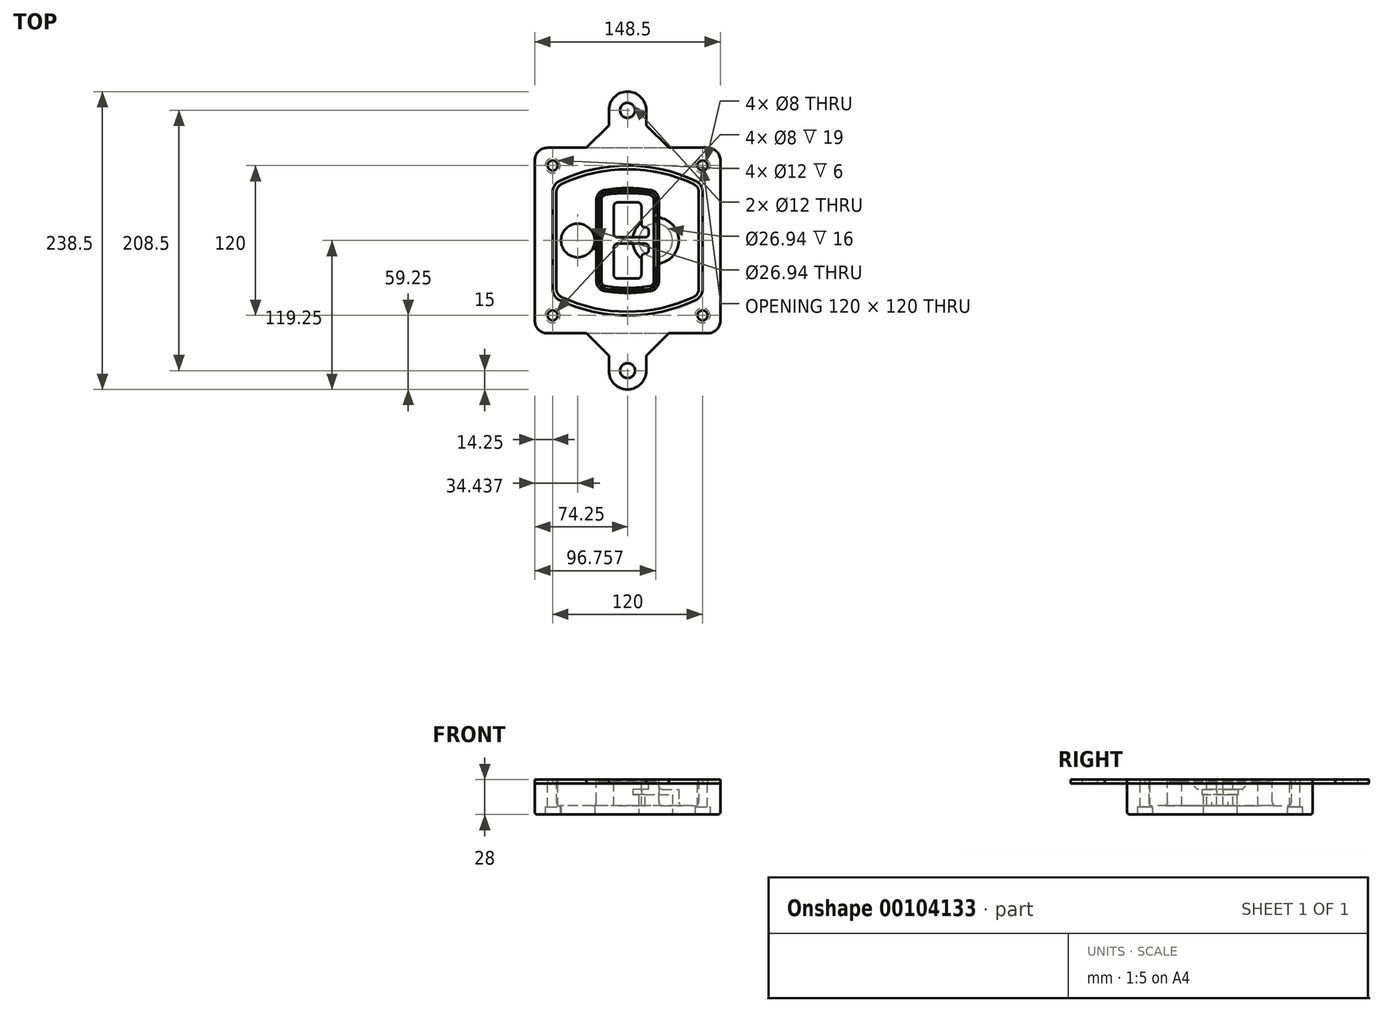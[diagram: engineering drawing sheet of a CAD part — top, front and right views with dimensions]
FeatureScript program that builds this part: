
annotation { "Feature Type Name" : "Feature", "Feature Type Description" : "" }
export const myFeature = defineFeature(function(context is Context, id is Id, definition is map)
    precondition{}
    {
        {
            var Q0;
            Q0=qCreatedBy(makeId("Top.planeOp"),FACE);
            var sketch = newSketch(context, id + "F0", { "sketchPlane" : qUnion([Q0])});
            skPoint(sketch, "E0.rect.middle", {"position": v(0, 0) * mm});
            skLineSegment(sketch, "E1.bottom", {"start": v(-64.25, -74.25) * mm, "end": v(64.25, -74.25) * mm});
            skLineSegment(sketch, "E1.top", {"start": v(-64.25, 74.25) * mm, "end": v(64.25, 74.25) * mm});
            skLineSegment(sketch, "E1.left", {"start": v(-74.25, -64.25) * mm, "end": v(-74.25, 64.25) * mm});
            skLineSegment(sketch, "E1.right", {"start": v(74.25, -64.25) * mm, "end": v(74.25, 64.25) * mm});
            skLineSegment(sketch, "E2", {"start": v(-74.25, 74.25) * mm, "end": v(74.25, -74.25) * mm, "construction": true});
            skLineSegment(sketch, "E3", {"start": v(74.25, 74.25) * mm, "end": v(-74.25, -74.25) * mm, "construction": true});
            skCircle(sketch, "E4", {"center": v(-60, 60) * mm, "radius": 4 * mm});
            skCircle(sketch, "E5", {"center": v(60, 60) * mm, "radius": 4 * mm});
            skCircle(sketch, "E6", {"center": v(60, -60) * mm, "radius": 4 * mm});
            skCircle(sketch, "E7", {"center": v(-60, -60) * mm, "radius": 4 * mm});
            skLineSegment(sketch, "E8", {"start": v(-60, 60) * mm, "end": v(60, 60) * mm, "construction": true});
            skLineSegment(sketch, "E9", {"start": v(60, 60) * mm, "end": v(60, -60) * mm, "construction": true});
            skLineSegment(sketch, "E10", {"start": v(60, -60) * mm, "end": v(-60, -60) * mm, "construction": true});
            skLineSegment(sketch, "E11", {"start": v(-60, -60) * mm, "end": v(-60, 60) * mm, "construction": true});
            skLineSegment(sketch, "E12", {"start": v(-60, 38.83) * mm, "end": v(-60, -38.83) * mm});
            skLineSegment(sketch, "E13", {"start": v(60, 38.83) * mm, "end": v(60, -38.83) * mm});
            skArc(sketch, "E14", {"start": v(54.26, 47.88) * mm, "mid": v(0, 60) * mm, "end": v(-54.26, 47.88) * mm});
            skArc(sketch, "E15", {"start": v(-54.26, -47.88) * mm, "mid": v(0, -60) * mm, "end": v(54.26, -47.88) * mm});
            skLineSegment(sketch, "E16", {"start": v(-60, 0) * mm, "end": v(60, 0) * mm, "construction": true});
            skPoint(sketch, "E17.visualSharp", {"position": v(-60, -45) * mm});
            skArc(sketch, "E17.filletArc", {"start": v(-60, -38.83) * mm, "mid": v(-58.44, -44.2) * mm, "end": v(-54.26, -47.88) * mm});
            skPoint(sketch, "E18.visualSharp", {"position": v(-60, 45) * mm});
            skArc(sketch, "E18.filletArc", {"start": v(-54.26, 47.88) * mm, "mid": v(-58.44, 44.2) * mm, "end": v(-60, 38.83) * mm});
            skPoint(sketch, "E19.visualSharp", {"position": v(60, 45) * mm});
            skArc(sketch, "E19.filletArc", {"start": v(60, 38.83) * mm, "mid": v(58.44, 44.2) * mm, "end": v(54.26, 47.88) * mm});
            skPoint(sketch, "E20.visualSharp", {"position": v(60, -45) * mm});
            skArc(sketch, "E20.filletArc", {"start": v(54.26, -47.88) * mm, "mid": v(58.44, -44.2) * mm, "end": v(60, -38.83) * mm});
            skPoint(sketch, "E21.visualSharp", {"position": v(-74.25, 74.25) * mm});
            skArc(sketch, "E21.filletArc", {"start": v(-64.25, 74.25) * mm, "mid": v(-71.32, 71.32) * mm, "end": v(-74.25, 64.25) * mm});
            skPoint(sketch, "E22.visualSharp", {"position": v(74.25, 74.25) * mm});
            skArc(sketch, "E22.filletArc", {"start": v(74.25, 64.25) * mm, "mid": v(71.32, 71.32) * mm, "end": v(64.25, 74.25) * mm});
            skPoint(sketch, "E23.visualSharp", {"position": v(74.25, -74.25) * mm});
            skArc(sketch, "E23.filletArc", {"start": v(64.25, -74.25) * mm, "mid": v(71.32, -71.32) * mm, "end": v(74.25, -64.25) * mm});
            skPoint(sketch, "E24.visualSharp", {"position": v(-74.25, -74.25) * mm});
            skArc(sketch, "E24.filletArc", {"start": v(-74.25, -64.25) * mm, "mid": v(-71.32, -71.32) * mm, "end": v(-64.25, -74.25) * mm});
            skArc(sketch, "E25.0", {"start": v(57, 38.83) * mm, "mid": v(55.9, 42.58) * mm, "end": v(52.98, 45.17) * mm});
            skLineSegment(sketch, "E25.1", {"start": v(57, 38.83) * mm, "end": v(57, -38.83) * mm});
            skArc(sketch, "E25.2", {"start": v(52.98, -45.17) * mm, "mid": v(55.9, -42.58) * mm, "end": v(57, -38.83) * mm});
            skArc(sketch, "E25.3", {"start": v(-52.98, -45.17) * mm, "mid": v(0, -57) * mm, "end": v(52.98, -45.17) * mm});
            skArc(sketch, "E25.4", {"start": v(-57, -38.83) * mm, "mid": v(-55.9, -42.58) * mm, "end": v(-52.98, -45.17) * mm});
            skArc(sketch, "E25.5", {"start": v(52.98, 45.17) * mm, "mid": v(0, 57) * mm, "end": v(-52.98, 45.17) * mm});
            skLineSegment(sketch, "E25.6", {"start": v(-57, 38.83) * mm, "end": v(-57, -38.83) * mm});
            skArc(sketch, "E25.7", {"start": v(-52.98, 45.17) * mm, "mid": v(-55.9, 42.58) * mm, "end": v(-57, 38.83) * mm});
            skArc(sketch, "E26.0", {"start": v(-55.96, 51.5) * mm, "mid": v(-61.82, 46.33) * mm, "end": v(-64, 38.83) * mm});
            skArc(sketch, "E26.1", {"start": v(55.96, 51.5) * mm, "mid": v(0, 64) * mm, "end": v(-55.96, 51.5) * mm});
            skArc(sketch, "E26.2", {"start": v(64, 38.83) * mm, "mid": v(61.82, 46.33) * mm, "end": v(55.96, 51.5) * mm});
            skLineSegment(sketch, "E26.3", {"start": v(64, 38.83) * mm, "end": v(64, -38.83) * mm});
            skArc(sketch, "E26.4", {"start": v(55.96, -51.5) * mm, "mid": v(61.82, -46.33) * mm, "end": v(64, -38.83) * mm});
            skLineSegment(sketch, "E26.5", {"start": v(-64, 38.83) * mm, "end": v(-64, -38.83) * mm});
            skArc(sketch, "E26.6", {"start": v(-55.96, -51.5) * mm, "mid": v(0, -64) * mm, "end": v(55.96, -51.5) * mm});
            skArc(sketch, "E26.7", {"start": v(-64, -38.83) * mm, "mid": v(-61.82, -46.33) * mm, "end": v(-55.96, -51.5) * mm});
            skSolve(sketch);
        }
        {
            var Q0;
            Q0=makeQuery(id+"F0.imprint","IMPRINT",FACE,{"disambiguationData":[TD([[makeQuery(id+"F0.imprint","IMPRINT",EDGE,{"derivedFrom":sQuery(id+"F0.wireOp",EDGE,"E1.bottom")}),1.0]])]});
            var Q1;
            Q1=makeQuery(id+"F0.imprint","IMPRINT",FACE,{"disambiguationData":[TD([[makeQuery(id+"F0.imprint","IMPRINT",EDGE,{"derivedFrom":sQuery(id+"F0.wireOp",EDGE,"E12")}),1.0]])]});
            var Q2;
            Q2=makeQuery(id+"F0.imprint","IMPRINT",FACE,{"disambiguationData":[TD([[makeQuery(id+"F0.imprint","IMPRINT",EDGE,{"derivedFrom":sQuery(id+"F0.wireOp",EDGE,"E25.0")}),1.0]])]});
            var Q3;
            Q3=makeQuery(id+"F0.imprint","IMPRINT",FACE,{"disambiguationData":[TD([[makeQuery(id+"F0.imprint","IMPRINT",EDGE,{"derivedFrom":sQuery(id+"F0.wireOp",EDGE,"E12")}),-1.0]])]});
            extrude(context, id + "F1", {"entities" : qUnion([Q0, Q1, Q2, Q3]), "oppositeDirection" : true, "depth" : 25 * mm});
        }
        {
            var Q0;
            Q0=makeQuery(id+"F0.imprint","IMPRINT",FACE,{"disambiguationData":[TD([[makeQuery(id+"F0.imprint","IMPRINT",EDGE,{"derivedFrom":sQuery(id+"F0.wireOp",EDGE,"E12")}),1.0]])]});
            extrude(context, id + "F2", {"entities" : qUnion([Q0]), "operationType" : NewBodyOperationType.ADD, "depth" : 3 * mm});
        }
        {
            var Q0;
            Q0=makeQuery(id+"F0.imprint","IMPRINT",FACE,{"disambiguationData":[TD([[makeQuery(id+"F0.imprint","IMPRINT",EDGE,{"derivedFrom":sQuery(id+"F0.wireOp",EDGE,"E25.0")}),1.0]])]});
            extrude(context, id + "F3", {"entities" : qUnion([Q0]), "operationType" : NewBodyOperationType.REMOVE, "oppositeDirection" : true, "depth" : 18 * mm});
        }
        {
            var Q0;
            Q0=makeQuery(id+"F2.opExtrude","CAP_FACE",FACE,{"disambiguationData":[OSD([sQuery(id+"F0.wireOp",EDGE,"E12"),sQuery(id+"F0.wireOp",EDGE,"E13"),sQuery(id+"F0.wireOp",EDGE,"E14"),sQuery(id+"F0.wireOp",EDGE,"E15"),sQuery(id+"F0.wireOp",EDGE,"E17.filletArc"),sQuery(id+"F0.wireOp",EDGE,"E18.filletArc"),sQuery(id+"F0.wireOp",EDGE,"E19.filletArc"),sQuery(id+"F0.wireOp",EDGE,"E20.filletArc"),sQuery(id+"F0.wireOp",EDGE,"E25.0"),sQuery(id+"F0.wireOp",EDGE,"E25.1"),sQuery(id+"F0.wireOp",EDGE,"E25.2"),sQuery(id+"F0.wireOp",EDGE,"E25.3"),sQuery(id+"F0.wireOp",EDGE,"E25.4"),sQuery(id+"F0.wireOp",EDGE,"E25.5"),sQuery(id+"F0.wireOp",EDGE,"E25.6"),sQuery(id+"F0.wireOp",EDGE,"E25.7")])],"isStart":false});
            var sketch = newSketch(context, id + "F4", { "sketchPlane" : qUnion([Q0])});
            skArc(sketch, "E27.0", {"start": v(-18.34, -40.45) * mm, "mid": v(0, -42) * mm, "end": v(18.34, -40.45) * mm});
            skArc(sketch, "E28.0", {"start": v(18.34, 40.45) * mm, "mid": v(0, 42) * mm, "end": v(-18.34, 40.45) * mm});
            skLineSegment(sketch, "E29", {"start": v(-25, 32.57) * mm, "end": v(-25, -32.57) * mm});
            skLineSegment(sketch, "E30", {"start": v(25, 32.57) * mm, "end": v(25, -32.57) * mm});
            skLineSegment(sketch, "E31", {"start": v(-25, 39.1) * mm, "end": v(25, 39.1) * mm, "construction": true});
            skLineSegment(sketch, "E32", {"start": v(-25, -39.1) * mm, "end": v(25, -39.1) * mm, "construction": true});
            skPoint(sketch, "E33.visualSharp", {"position": v(-25, 39.1) * mm});
            skArc(sketch, "E33.filletArc", {"start": v(-18.34, 40.45) * mm, "mid": v(-23.11, 37.73) * mm, "end": v(-25, 32.57) * mm});
            skPoint(sketch, "E34.visualSharp", {"position": v(25, 39.1) * mm});
            skArc(sketch, "E34.filletArc", {"start": v(25, 32.57) * mm, "mid": v(23.11, 37.73) * mm, "end": v(18.34, 40.45) * mm});
            skPoint(sketch, "E35.visualSharp", {"position": v(25, -39.1) * mm});
            skArc(sketch, "E35.filletArc", {"start": v(18.34, -40.45) * mm, "mid": v(23.11, -37.73) * mm, "end": v(25, -32.57) * mm});
            skPoint(sketch, "E36.visualSharp", {"position": v(-25, -39.1) * mm});
            skArc(sketch, "E36.filletArc", {"start": v(-25, -32.57) * mm, "mid": v(-23.11, -37.73) * mm, "end": v(-18.34, -40.45) * mm});
            skArc(sketch, "E37.0", {"start": v(52.98, 45.17) * mm, "mid": v(0, 57) * mm, "end": v(-52.98, 45.17) * mm});
            skArc(sketch, "E37.1", {"start": v(-52.98, 45.17) * mm, "mid": v(-55.9, 42.58) * mm, "end": v(-57, 38.83) * mm});
            skLineSegment(sketch, "E37.2", {"start": v(-57, 38.83) * mm, "end": v(-57, -38.83) * mm});
            skArc(sketch, "E37.3", {"start": v(-57, -38.83) * mm, "mid": v(-55.9, -42.58) * mm, "end": v(-52.98, -45.17) * mm});
            skArc(sketch, "E37.4", {"start": v(-52.98, -45.17) * mm, "mid": v(0, -57) * mm, "end": v(52.98, -45.17) * mm});
            skArc(sketch, "E37.5", {"start": v(52.98, -45.17) * mm, "mid": v(55.9, -42.58) * mm, "end": v(57, -38.83) * mm});
            skLineSegment(sketch, "E37.6", {"start": v(57, 38.83) * mm, "end": v(57, -38.83) * mm});
            skArc(sketch, "E37.7", {"start": v(57, 38.83) * mm, "mid": v(55.9, 42.58) * mm, "end": v(52.98, 45.17) * mm});
            skLineSegment(sketch, "E38.0", {"start": v(23, 32.57) * mm, "end": v(23, -32.57) * mm});
            skArc(sketch, "E38.1", {"start": v(18, -38.48) * mm, "mid": v(21.58, -36.44) * mm, "end": v(23, -32.57) * mm});
            skArc(sketch, "E38.2", {"start": v(-18, -38.48) * mm, "mid": v(0, -40) * mm, "end": v(18, -38.48) * mm});
            skArc(sketch, "E38.3", {"start": v(-23, -32.57) * mm, "mid": v(-21.58, -36.44) * mm, "end": v(-18, -38.48) * mm});
            skLineSegment(sketch, "E38.4", {"start": v(-23, 32.57) * mm, "end": v(-23, -32.57) * mm});
            skArc(sketch, "E38.5", {"start": v(23, 32.57) * mm, "mid": v(21.58, 36.44) * mm, "end": v(18, 38.48) * mm});
            skArc(sketch, "E38.6", {"start": v(-18, 38.48) * mm, "mid": v(-21.58, 36.44) * mm, "end": v(-23, 32.57) * mm});
            skArc(sketch, "E38.7", {"start": v(18, 38.48) * mm, "mid": v(0, 40) * mm, "end": v(-18, 38.48) * mm});
            skArc(sketch, "E39.0", {"start": v(21, 32.57) * mm, "mid": v(20.06, 35.15) * mm, "end": v(17.67, 36.5) * mm});
            skLineSegment(sketch, "E39.1", {"start": v(21, 32.57) * mm, "end": v(21, -32.57) * mm});
            skArc(sketch, "E39.2", {"start": v(17.67, -36.5) * mm, "mid": v(20.06, -35.15) * mm, "end": v(21, -32.57) * mm});
            skArc(sketch, "E39.3", {"start": v(-17.67, -36.5) * mm, "mid": v(0, -38) * mm, "end": v(17.67, -36.5) * mm});
            skArc(sketch, "E39.4", {"start": v(-21, -32.57) * mm, "mid": v(-20.06, -35.15) * mm, "end": v(-17.67, -36.5) * mm});
            skArc(sketch, "E39.5", {"start": v(17.67, 36.5) * mm, "mid": v(0, 38) * mm, "end": v(-17.67, 36.5) * mm});
            skLineSegment(sketch, "E39.6", {"start": v(-21, 32.57) * mm, "end": v(-21, -32.57) * mm});
            skArc(sketch, "E39.7", {"start": v(-17.67, 36.5) * mm, "mid": v(-20.06, 35.15) * mm, "end": v(-21, 32.57) * mm});
            skLineSegment(sketch, "E40", {"start": v(-25, 0) * mm, "end": v(25, 0) * mm, "construction": true});
            skLineSegment(sketch, "E41", {"start": v(-11, 5.5) * mm, "end": v(-11, 27.5) * mm});
            skLineSegment(sketch, "E42", {"start": v(-8, 30.5) * mm, "end": v(8, 30.5) * mm});
            skLineSegment(sketch, "E43", {"start": v(11, 27.5) * mm, "end": v(11, 13.5) * mm});
            skLineSegment(sketch, "E44", {"start": v(14, 10.5) * mm, "end": v(14, 10.5) * mm});
            skLineSegment(sketch, "E45", {"start": v(17, 7.5) * mm, "end": v(17, 5.5) * mm});
            skLineSegment(sketch, "E46", {"start": v(14, 2.5) * mm, "end": v(-8, 2.5) * mm});
            skPoint(sketch, "E47.visualSharp", {"position": v(-11, 30.5) * mm});
            skArc(sketch, "E47.filletArc", {"start": v(-8, 30.5) * mm, "mid": v(-10.12, 29.62) * mm, "end": v(-11, 27.5) * mm});
            skPoint(sketch, "E48.visualSharp", {"position": v(11, 30.5) * mm});
            skArc(sketch, "E48.filletArc", {"start": v(11, 27.5) * mm, "mid": v(10.12, 29.62) * mm, "end": v(8, 30.5) * mm});
            skPoint(sketch, "E49.visualSharp", {"position": v(11, 10.5) * mm});
            skArc(sketch, "E49.filletArc", {"start": v(11, 13.5) * mm, "mid": v(11.88, 11.38) * mm, "end": v(14, 10.5) * mm});
            skPoint(sketch, "E50.visualSharp", {"position": v(17, 10.5) * mm});
            skArc(sketch, "E50.filletArc", {"start": v(17, 7.5) * mm, "mid": v(16.12, 9.62) * mm, "end": v(14, 10.5) * mm});
            skPoint(sketch, "E51.visualSharp", {"position": v(17, 2.5) * mm});
            skArc(sketch, "E51.filletArc", {"start": v(14, 2.5) * mm, "mid": v(16.12, 3.38) * mm, "end": v(17, 5.5) * mm});
            skPoint(sketch, "E52.visualSharp", {"position": v(-11, 2.5) * mm});
            skArc(sketch, "E52.filletArc", {"start": v(-11, 5.5) * mm, "mid": v(-10.12, 3.38) * mm, "end": v(-8, 2.5) * mm});
            skLineSegment(sketch, "E53.0.MirrorCS", {"start": v(14, -2.5) * mm, "end": v(-8, -2.5) * mm});
            skArc(sketch, "E54.0.MirrorCS", {"start": v(-11, -5.5) * mm, "mid": v(-10.12, -3.38) * mm, "end": v(-8, -2.5) * mm});
            skLineSegment(sketch, "E55.0.MirrorCS", {"start": v(-11, -5.5) * mm, "end": v(-11, -27.5) * mm});
            skArc(sketch, "E56.0.MirrorCS", {"start": v(-8, -30.5) * mm, "mid": v(-10.12, -29.62) * mm, "end": v(-11, -27.5) * mm});
            skLineSegment(sketch, "E57.0.MirrorCS", {"start": v(-8, -30.5) * mm, "end": v(8, -30.5) * mm});
            skArc(sketch, "E58.0.MirrorCS", {"start": v(11, -27.5) * mm, "mid": v(10.12, -29.62) * mm, "end": v(8, -30.5) * mm});
            skLineSegment(sketch, "E59.0.MirrorCS", {"start": v(11, -27.5) * mm, "end": v(11, -13.5) * mm});
            skArc(sketch, "E60.0.MirrorCS", {"start": v(11, -13.5) * mm, "mid": v(11.88, -11.38) * mm, "end": v(14, -10.5) * mm});
            skArc(sketch, "E61.0.MirrorCS", {"start": v(17, -7.5) * mm, "mid": v(16.12, -9.62) * mm, "end": v(14, -10.5) * mm});
            skLineSegment(sketch, "E62.0.MirrorCS", {"start": v(17, -7.5) * mm, "end": v(17, -5.5) * mm});
            skArc(sketch, "E63.0.MirrorCS", {"start": v(14, -2.5) * mm, "mid": v(16.12, -3.38) * mm, "end": v(17, -5.5) * mm});
            skSolve(sketch);
        }
        {
            var Q0;
            Q0=makeQuery(id+"F4.imprint","IMPRINT",FACE,{"disambiguationData":[TD([[makeQuery(id+"F4.imprint","IMPRINT",EDGE,{"derivedFrom":sQuery(id+"F4.wireOp",EDGE,"E27.0")}),1.0]])]});
            var Q1;
            Q1=makeQuery(id+"F4.imprint","IMPRINT",FACE,{"disambiguationData":[TD([[makeQuery(id+"F4.imprint","IMPRINT",EDGE,{"derivedFrom":sQuery(id+"F4.wireOp",EDGE,"E38.0")}),-1.0]])]});
            var Q2;
            Q2=makeQuery(id+"F4.imprint","IMPRINT",FACE,{"disambiguationData":[TD([[makeQuery(id+"F4.imprint","IMPRINT",EDGE,{"derivedFrom":sQuery(id+"F4.wireOp",EDGE,"E39.0")}),1.0]])]});
            extrude(context, id + "F5", {"entities" : qUnion([Q0, Q1, Q2]), "operationType" : NewBodyOperationType.ADD, "endBound" : BoundingType.UP_TO_NEXT, "oppositeDirection" : true, "depth" : 25 * mm});
        }
        {
            var Q0;
            Q0=makeQuery(id+"F4.imprint","IMPRINT",FACE,{"disambiguationData":[TD([[makeQuery(id+"F4.imprint","IMPRINT",EDGE,{"derivedFrom":sQuery(id+"F4.wireOp",EDGE,"E38.0")}),-1.0]])]});
            extrude(context, id + "F6", {"entities" : qUnion([Q0]), "operationType" : NewBodyOperationType.REMOVE, "oppositeDirection" : true, "depth" : 2 * mm});
        }
        {
            var Q0;
            Q0=makeQuery(id+"F1.opExtrude","CAP_FACE",FACE,{"disambiguationData":[OSD([sQuery(id+"F0.wireOp",EDGE,"E1.bottom"),sQuery(id+"F0.wireOp",EDGE,"E1.top"),sQuery(id+"F0.wireOp",EDGE,"E1.left"),sQuery(id+"F0.wireOp",EDGE,"E1.right"),sQuery(id+"F0.wireOp",EDGE,"E4"),sQuery(id+"F0.wireOp",EDGE,"E5"),sQuery(id+"F0.wireOp",EDGE,"E6"),sQuery(id+"F0.wireOp",EDGE,"E7"),sQuery(id+"F0.wireOp",EDGE,"E21.filletArc"),sQuery(id+"F0.wireOp",EDGE,"E22.filletArc"),sQuery(id+"F0.wireOp",EDGE,"E23.filletArc"),sQuery(id+"F0.wireOp",EDGE,"E24.filletArc")])],"isStart":false});
            var sketch = newSketch(context, id + "F7", { "sketchPlane" : qUnion([Q0])});
            skCircle(sketch, "E64", {"center": v(22.5, 0) * mm, "radius": 13.47 * mm});
            skCircle(sketch, "E65", {"center": v(-39.81, 0) * mm, "radius": 13.47 * mm});
            skLineSegment(sketch, "E66", {"start": v(74.25, 0) * mm, "end": v(-74.25, 0) * mm});
            skCircle(sketch, "E67", {"center": v(22.5, 0) * mm, "radius": 18.47 * mm});
            skCircle(sketch, "E68", {"center": v(60, -60) * mm, "radius": 6 * mm});
            skCircle(sketch, "E69", {"center": v(-60, -60) * mm, "radius": 6 * mm});
            skCircle(sketch, "E70", {"center": v(-60, 60) * mm, "radius": 6 * mm});
            skCircle(sketch, "E71", {"center": v(60, 60) * mm, "radius": 6 * mm});
            skSolve(sketch);
        }
        {
            var Q0;
            {var subQ1=sQuery(id+"F7.wireOp",EDGE,"E66");var subQ4=sQuery(id+"F7.wireOp",EDGE,"E64");var subQ6=makeQuery(id+"F7.imprint","INTERSECT",VERTEX,{"disambiguationData":[OD(0.0)],"derivedFrom":[subQ4,subQ1]});Q0=makeQuery(id+"F7.imprint","IMPRINT",FACE,{"disambiguationData":[TD([[makeQuery(id+"F7.imprint","IMPRINT",EDGE,{"disambiguationData":[TD([[subQ6,-1.0]])],"derivedFrom":subQ4}),-1.0]])]});}
            var Q1;
            {var subQ0=sQuery(id+"F7.wireOp",EDGE,"E66");var subQ1=sQuery(id+"F7.wireOp",EDGE,"E64");var subQ3=makeQuery(id+"F7.imprint","INTERSECT",VERTEX,{"disambiguationData":[OD(0.0)],"derivedFrom":[subQ1,subQ0]});Q1=makeQuery(id+"F7.imprint","IMPRINT",FACE,{"disambiguationData":[TD([[makeQuery(id+"F7.imprint","IMPRINT",EDGE,{"disambiguationData":[TD([[subQ3,-1.0]])],"derivedFrom":subQ1}),1.0]])]});}
            var Q2;
            {var subQ0=sQuery(id+"F7.wireOp",EDGE,"E66");var subQ1=sQuery(id+"F7.wireOp",EDGE,"E64");var subQ3=makeQuery(id+"F7.imprint","INTERSECT",VERTEX,{"disambiguationData":[OD(0.0)],"derivedFrom":[subQ1,subQ0]});Q2=makeQuery(id+"F7.imprint","IMPRINT",FACE,{"disambiguationData":[TD([[makeQuery(id+"F7.imprint","IMPRINT",EDGE,{"disambiguationData":[TD([[subQ3,1.0]])],"derivedFrom":subQ1}),1.0]])]});}
            var Q3;
            {var subQ1=sQuery(id+"F7.wireOp",EDGE,"E66");var subQ4=sQuery(id+"F7.wireOp",EDGE,"E64");var subQ6=makeQuery(id+"F7.imprint","INTERSECT",VERTEX,{"disambiguationData":[OD(0.0)],"derivedFrom":[subQ4,subQ1]});Q3=makeQuery(id+"F7.imprint","IMPRINT",FACE,{"disambiguationData":[TD([[makeQuery(id+"F7.imprint","IMPRINT",EDGE,{"disambiguationData":[TD([[subQ6,1.0]])],"derivedFrom":subQ4}),-1.0]])]});}
            extrude(context, id + "F8", {"entities" : qUnion([Q0, Q1, Q2, Q3]), "operationType" : NewBodyOperationType.ADD, "oppositeDirection" : true, "depth" : 20 * mm});
        }
        {
            var Q0;
            {var subQ0=sQuery(id+"F7.wireOp",EDGE,"E66");var subQ1=sQuery(id+"F7.wireOp",EDGE,"E64");var subQ3=makeQuery(id+"F7.imprint","INTERSECT",VERTEX,{"disambiguationData":[OD(0.0)],"derivedFrom":[subQ1,subQ0]});Q0=makeQuery(id+"F7.imprint","IMPRINT",FACE,{"disambiguationData":[TD([[makeQuery(id+"F7.imprint","IMPRINT",EDGE,{"disambiguationData":[TD([[subQ3,-1.0]])],"derivedFrom":subQ1}),1.0]])]});}
            var Q1;
            {var subQ0=sQuery(id+"F7.wireOp",EDGE,"E66");var subQ1=sQuery(id+"F7.wireOp",EDGE,"E64");var subQ3=makeQuery(id+"F7.imprint","INTERSECT",VERTEX,{"disambiguationData":[OD(0.0)],"derivedFrom":[subQ1,subQ0]});Q1=makeQuery(id+"F7.imprint","IMPRINT",FACE,{"disambiguationData":[TD([[makeQuery(id+"F7.imprint","IMPRINT",EDGE,{"disambiguationData":[TD([[subQ3,1.0]])],"derivedFrom":subQ1}),1.0]])]});}
            extrude(context, id + "F9", {"entities" : qUnion([Q0, Q1]), "operationType" : NewBodyOperationType.REMOVE, "oppositeDirection" : true, "depth" : 16 * mm});
        }
        {
            var Q0;
            {var subQ0=sQuery(id+"F7.wireOp",EDGE,"E66");var subQ1=sQuery(id+"F7.wireOp",EDGE,"E65");var subQ3=makeQuery(id+"F7.imprint","INTERSECT",VERTEX,{"disambiguationData":[OD(0.0)],"derivedFrom":[subQ1,subQ0]});Q0=makeQuery(id+"F7.imprint","IMPRINT",FACE,{"disambiguationData":[TD([[makeQuery(id+"F7.imprint","IMPRINT",EDGE,{"disambiguationData":[TD([[subQ3,-1.0]])],"derivedFrom":subQ1}),1.0]])]});}
            var Q1;
            {var subQ0=sQuery(id+"F7.wireOp",EDGE,"E66");var subQ1=sQuery(id+"F7.wireOp",EDGE,"E65");var subQ3=makeQuery(id+"F7.imprint","INTERSECT",VERTEX,{"disambiguationData":[OD(0.0)],"derivedFrom":[subQ1,subQ0]});Q1=makeQuery(id+"F7.imprint","IMPRINT",FACE,{"disambiguationData":[TD([[makeQuery(id+"F7.imprint","IMPRINT",EDGE,{"disambiguationData":[TD([[subQ3,1.0]])],"derivedFrom":subQ1}),1.0]])]});}
            extrude(context, id + "F10", {"entities" : qUnion([Q0, Q1]), "operationType" : NewBodyOperationType.REMOVE, "oppositeDirection" : true, "depth" : 25 * mm});
        }
        {
            var Q0;
            Q0=makeQuery(id+"F7.imprint","IMPRINT",FACE,{"disambiguationData":[TD([[makeQuery(id+"F7.imprint","IMPRINT",EDGE,{"derivedFrom":sQuery(id+"F7.wireOp",EDGE,"E68")}),1.0]])]});
            var Q1;
            Q1=makeQuery(id+"F7.imprint","IMPRINT",FACE,{"disambiguationData":[TD([[makeQuery(id+"F7.imprint","IMPRINT",EDGE,{"derivedFrom":makeQuery(id+"F1.opExtrude","CAP_EDGE",EDGE,{"disambiguationData":[OSD([sQuery(id+"F0.wireOp",EDGE,"E5")])],"isStart":false})}),-1.0]])]});
            var Q2;
            Q2=makeQuery(id+"F7.imprint","IMPRINT",FACE,{"disambiguationData":[TD([[makeQuery(id+"F7.imprint","IMPRINT",EDGE,{"derivedFrom":sQuery(id+"F7.wireOp",EDGE,"E69")}),1.0]])]});
            var Q3;
            Q3=makeQuery(id+"F7.imprint","IMPRINT",FACE,{"disambiguationData":[TD([[makeQuery(id+"F7.imprint","IMPRINT",EDGE,{"derivedFrom":makeQuery(id+"F1.opExtrude","CAP_EDGE",EDGE,{"disambiguationData":[OSD([sQuery(id+"F0.wireOp",EDGE,"E4")])],"isStart":false})}),-1.0]])]});
            var Q4;
            Q4=makeQuery(id+"F7.imprint","IMPRINT",FACE,{"disambiguationData":[TD([[makeQuery(id+"F7.imprint","IMPRINT",EDGE,{"derivedFrom":sQuery(id+"F7.wireOp",EDGE,"E70")}),1.0]])]});
            var Q5;
            Q5=makeQuery(id+"F7.imprint","IMPRINT",FACE,{"disambiguationData":[TD([[makeQuery(id+"F7.imprint","IMPRINT",EDGE,{"derivedFrom":makeQuery(id+"F1.opExtrude","CAP_EDGE",EDGE,{"disambiguationData":[OSD([sQuery(id+"F0.wireOp",EDGE,"E7")])],"isStart":false})}),-1.0]])]});
            var Q6;
            Q6=makeQuery(id+"F7.imprint","IMPRINT",FACE,{"disambiguationData":[TD([[makeQuery(id+"F7.imprint","IMPRINT",EDGE,{"derivedFrom":sQuery(id+"F7.wireOp",EDGE,"E71")}),1.0]])]});
            var Q7;
            Q7=makeQuery(id+"F7.imprint","IMPRINT",FACE,{"disambiguationData":[TD([[makeQuery(id+"F7.imprint","IMPRINT",EDGE,{"derivedFrom":makeQuery(id+"F1.opExtrude","CAP_EDGE",EDGE,{"disambiguationData":[OSD([sQuery(id+"F0.wireOp",EDGE,"E6")])],"isStart":false})}),-1.0]])]});
            extrude(context, id + "F11", {"entities" : qUnion([Q0, Q1, Q2, Q3, Q4, Q5, Q6, Q7]), "operationType" : NewBodyOperationType.REMOVE, "oppositeDirection" : true, "depth" : 6 * mm});
        }
        {
            var Q0;
            Q0=makeQuery(id+"F9.boolean.opBoolean","COPY",FACE,{"derivedFrom":makeQuery(id+"F9.opExtrude","CAP_FACE",FACE,{"disambiguationData":[OSD([sQuery(id+"F7.wireOp",EDGE,"E64")])],"isStart":false})});
            var sketch = newSketch(context, id + "F12", { "sketchPlane" : qUnion([Q0])});
            skArc(sketch, "E72.0", {"start": v(11, 14.45) * mm, "mid": v(6.45, 9.13) * mm, "end": v(4.2, 2.5) * mm});
            skArc(sketch, "E72.1", {"start": v(4.2, -2.5) * mm, "mid": v(6.45, -9.13) * mm, "end": v(11, -14.45) * mm});
            skLineSegment(sketch, "E73", {"start": v(4.2, -2.5) * mm, "end": v(14, -2.5) * mm});
            skLineSegment(sketch, "E74.0", {"start": v(14, 2.5) * mm, "end": v(4.2, 2.5) * mm});
            skArc(sketch, "E74.1", {"start": v(14, 2.5) * mm, "mid": v(16.12, 3.38) * mm, "end": v(17, 5.5) * mm});
            skLineSegment(sketch, "E74.2", {"start": v(17, 7.5) * mm, "end": v(17, 5.5) * mm});
            skArc(sketch, "E74.3", {"start": v(17, 7.5) * mm, "mid": v(16.12, 9.62) * mm, "end": v(14, 10.5) * mm});
            skArc(sketch, "E74.4", {"start": v(11, 13.5) * mm, "mid": v(11.88, 11.38) * mm, "end": v(14, 10.5) * mm});
            skLineSegment(sketch, "E74.5", {"start": v(11, 14.45) * mm, "end": v(11, 13.5) * mm});
            skLineSegment(sketch, "E74.7", {"start": v(14, -2.5) * mm, "end": v(4.2, -2.5) * mm});
            skArc(sketch, "E74.8", {"start": v(14, -2.5) * mm, "mid": v(16.12, -3.38) * mm, "end": v(17, -5.5) * mm});
            skLineSegment(sketch, "E74.9", {"start": v(17, -7.5) * mm, "end": v(17, -5.5) * mm});
            skArc(sketch, "E74.10", {"start": v(17, -7.5) * mm, "mid": v(16.12, -9.62) * mm, "end": v(14, -10.5) * mm});
            skArc(sketch, "E74.11", {"start": v(11, -13.5) * mm, "mid": v(11.88, -11.38) * mm, "end": v(14, -10.5) * mm});
            skLineSegment(sketch, "E74.12", {"start": v(11, -14.45) * mm, "end": v(11, -13.5) * mm});
            skPoint(sketch, "E75.orphan", {"position": v(11, -27.5) * mm});
            skPoint(sketch, "E76.orphan", {"position": v(-8, -2.5) * mm});
            skPoint(sketch, "E77.orphan", {"position": v(-8, 2.5) * mm});
            skPoint(sketch, "E78.orphan", {"position": v(11, 27.5) * mm});
            skSolve(sketch);
        }
        {
            var Q0;
            {var subQ7=sQuery(id+"F12.wireOp",EDGE,"E72.0");var subQ14=sQuery(id+"F12.wireOp",EDGE,"E72.1");var subQ16=sQuery(id+"F12.wireOp",EDGE,"E74.1");var subQ18=sQuery(id+"F12.wireOp",EDGE,"E74.8");Q0=qUnion([makeQuery(id+"F12.imprint","IMPRINT",FACE,{"disambiguationData":[TD([[makeQuery(id+"F12.imprint","IMPRINT",EDGE,{"derivedFrom":subQ7}),1.0]])]}),makeQuery(id+"F12.imprint","IMPRINT",FACE,{"disambiguationData":[TD([[makeQuery(id+"F12.imprint","IMPRINT",EDGE,{"derivedFrom":subQ14}),1.0]])]}),makeQuery(id+"F12.imprint","IMPRINT",FACE,{"disambiguationData":[TD([[makeQuery(id+"F12.imprint","IMPRINT",EDGE,{"derivedFrom":subQ16}),1.0]])]}),makeQuery(id+"F12.imprint","IMPRINT",FACE,{"disambiguationData":[TD([[makeQuery(id+"F12.imprint","IMPRINT",EDGE,{"derivedFrom":subQ18}),-1.0]])]})]);}
            var Q1;
            Q1=makeQuery(id+"F5.boolean.opBoolean","SPLIT",FACE,{"disambiguationData":[TD([makeQuery(id+"F5.opExtrude","SWEPT_FACE",FACE,{"disambiguationData":[OSD([sQuery(id+"F4.wireOp",EDGE,"E41")])]})])],"derivedFrom":makeQuery(id+"F3.boolean.opBoolean","COPY",FACE,{"derivedFrom":makeQuery(id+"F3.opExtrude","CAP_FACE",FACE,{"disambiguationData":[OSD([sQuery(id+"F0.wireOp",EDGE,"E25.0"),sQuery(id+"F0.wireOp",EDGE,"E25.1"),sQuery(id+"F0.wireOp",EDGE,"E25.2"),sQuery(id+"F0.wireOp",EDGE,"E25.3"),sQuery(id+"F0.wireOp",EDGE,"E25.4"),sQuery(id+"F0.wireOp",EDGE,"E25.5"),sQuery(id+"F0.wireOp",EDGE,"E25.6"),sQuery(id+"F0.wireOp",EDGE,"E25.7")])],"isStart":false})})});
            extrude(context, id + "F13", {"entities" : qUnion([Q0]), "operationType" : NewBodyOperationType.REMOVE, "endBound" : BoundingType.UP_TO_SURFACE, "endBoundEntityFace" : qUnion([Q1]), "depth" : 25 * mm});
        }
        {
            var Q0;
            Q0=makeQuery(id+"F3.boolean.opBoolean","COPY",EDGE,{"derivedFrom":makeQuery(id+"F3.opExtrude","CAP_EDGE",EDGE,{"disambiguationData":[OSD([sQuery(id+"F0.wireOp",EDGE,"E25.6")])],"isStart":false})});
            var Q1;
            Q1=makeQuery(id+"F8.boolean.opBoolean","INTERSECT",EDGE,{"derivedFrom":[makeQuery(id+"F5.opExtrude","SWEPT_FACE",FACE,{"disambiguationData":[OSD([sQuery(id+"F4.wireOp",EDGE,"E30")])]}),makeQuery(id+"F8.opExtrude","CAP_FACE",FACE,{"disambiguationData":[OSD([sQuery(id+"F7.wireOp",EDGE,"E67")])],"isStart":false})]});
            var Q2;
            Q2=makeQuery(id+"F8.boolean.opBoolean","INTERSECT",EDGE,{"disambiguationData":[OD(1.0)],"derivedFrom":[makeQuery(id+"F5.opExtrude","SWEPT_FACE",FACE,{"disambiguationData":[OSD([sQuery(id+"F4.wireOp",EDGE,"E30")])]}),makeQuery(id+"F8.opExtrude","SWEPT_FACE",FACE,{"disambiguationData":[OSD([sQuery(id+"F7.wireOp",EDGE,"E67")])]})]});
            var Q3;
            {var subQ0=sQuery(id+"F4.wireOp",EDGE,"E30");Q3=makeQuery(id+"F8.boolean.opBoolean","SPLIT",EDGE,{"disambiguationData":[TD([makeQuery(id+"F5.opExtrude","SWEPT_FACE",FACE,{"disambiguationData":[OSD([sQuery(id+"F4.wireOp",EDGE,"E35.filletArc")])]})])],"derivedFrom":makeQuery(id+"F5.opExtrude","CAP_EDGE",EDGE,{"disambiguationData":[OSD([subQ0])],"isStart":false})});}
            var Q4;
            {var subQ0=sQuery(id+"F0.wireOp",EDGE,"E25.7");var subQ1=sQuery(id+"F0.wireOp",EDGE,"E25.1");var subQ2=sQuery(id+"F0.wireOp",EDGE,"E25.6");var subQ3=sQuery(id+"F0.wireOp",EDGE,"E25.5");var subQ4=sQuery(id+"F0.wireOp",EDGE,"E25.4");var subQ5=sQuery(id+"F0.wireOp",EDGE,"E25.0");var subQ6=sQuery(id+"F0.wireOp",EDGE,"E25.2");var subQ7=sQuery(id+"F0.wireOp",EDGE,"E25.3");Q4=makeQuery(id+"F8.boolean.opBoolean","INTERSECT",EDGE,{"derivedFrom":[makeQuery(id+"F5.boolean.opBoolean","SPLIT",FACE,{"disambiguationData":[TD([makeQuery(id+"F2.opExtrude","SWEPT_FACE",FACE,{"disambiguationData":[OSD([subQ5])]})])],"derivedFrom":makeQuery(id+"F3.boolean.opBoolean","COPY",FACE,{"derivedFrom":makeQuery(id+"F3.opExtrude","CAP_FACE",FACE,{"disambiguationData":[OSD([subQ5,subQ1,subQ6,subQ7,subQ4,subQ3,subQ2,subQ0])],"isStart":false})})}),makeQuery(id+"F8.opExtrude","SWEPT_FACE",FACE,{"disambiguationData":[OSD([sQuery(id+"F7.wireOp",EDGE,"E67")])]})]});}
            var Q5;
            Q5=makeQuery(id+"F8.boolean.opBoolean","INTERSECT",EDGE,{"disambiguationData":[OD(0.0)],"derivedFrom":[makeQuery(id+"F5.opExtrude","SWEPT_FACE",FACE,{"disambiguationData":[OSD([sQuery(id+"F4.wireOp",EDGE,"E30")])]}),makeQuery(id+"F8.opExtrude","SWEPT_FACE",FACE,{"disambiguationData":[OSD([sQuery(id+"F7.wireOp",EDGE,"E67")])]})]});
            fillet(context, id + "F14", {"entities" : qUnion([Q0, Q1, Q2, Q3, Q4, Q5]), "radius" : 3 * mm, "tangentPropagation" : true, "allowEdgeOverflow" : false});
        }
        {
            var Q0;
            Q0=makeQuery(id+"F1.opExtrude","CAP_EDGE",EDGE,{"disambiguationData":[OSD([sQuery(id+"F0.wireOp",EDGE,"E1.bottom")])],"isStart":false});
            fillet(context, id + "F15", {"entities" : qUnion([Q0]), "radius" : 2 * mm, "tangentPropagation" : true, "allowEdgeOverflow" : false});
        }
        {
            var Q0;
            {var subQ0=sQuery(id+"F0.wireOp",EDGE,"E22.filletArc");var subQ1=sQuery(id+"F0.wireOp",EDGE,"E7");var subQ2=sQuery(id+"F0.wireOp",EDGE,"E6");var subQ3=sQuery(id+"F0.wireOp",EDGE,"E5");var subQ4=sQuery(id+"F0.wireOp",EDGE,"E4");var subQ5=sQuery(id+"F0.wireOp",EDGE,"E1.bottom");var subQ6=sQuery(id+"F0.wireOp",EDGE,"E21.filletArc");var subQ7=sQuery(id+"F0.wireOp",EDGE,"E1.top");var subQ8=sQuery(id+"F0.wireOp",EDGE,"E1.left");var subQ9=sQuery(id+"F0.wireOp",EDGE,"E1.right");var subQ10=sQuery(id+"F0.wireOp",EDGE,"E23.filletArc");var subQ11=sQuery(id+"F0.wireOp",EDGE,"E24.filletArc");Q0=makeQuery(id+"F2.boolean.opBoolean","SPLIT",FACE,{"disambiguationData":[TD([makeQuery(id+"F1.opExtrude","SWEPT_FACE",FACE,{"disambiguationData":[OSD([subQ5])]})])],"derivedFrom":makeQuery(id+"F1.opExtrude","CAP_FACE",FACE,{"disambiguationData":[OSD([subQ5,subQ7,subQ8,subQ9,subQ4,subQ3,subQ2,subQ1,subQ6,subQ0,subQ10,subQ11])],"isStart":true})});}
            var sketch = newSketch(context, id + "F16", { "sketchPlane" : qUnion([Q0])});
            skLineSegment(sketch, "E79", {"start": v(0, 74.25) * mm, "end": v(0, 104.25) * mm, "construction": true});
            skLineSegment(sketch, "E80", {"start": v(-33, 74.25) * mm, "end": v(-15, 92.25) * mm});
            skLineSegment(sketch, "E81", {"start": v(-15, 92.25) * mm, "end": v(-15, 104.25) * mm});
            skArc(sketch, "E82", {"start": v(15, 104.25) * mm, "mid": v(0, 119.25) * mm, "end": v(-15, 104.25) * mm});
            skLineSegment(sketch, "E83", {"start": v(15, 104.25) * mm, "end": v(15, 92.25) * mm});
            skLineSegment(sketch, "E84", {"start": v(33, 74.25) * mm, "end": v(15, 92.25) * mm});
            skCircle(sketch, "E85", {"center": v(0, 104.25) * mm, "radius": 6 * mm});
            skLineSegment(sketch, "E86", {"start": v(-74.25, 0) * mm, "end": v(74.25, 0) * mm, "construction": true});
            skLineSegment(sketch, "E87.MirrorCS", {"start": v(-33, -74.25) * mm, "end": v(-15, -92.25) * mm});
            skLineSegment(sketch, "E88.MirrorCS", {"start": v(-15, -92.25) * mm, "end": v(-15, -104.25) * mm});
            skArc(sketch, "E89.MirrorCS", {"start": v(15, -104.25) * mm, "mid": v(0, -119.25) * mm, "end": v(-15, -104.25) * mm});
            skLineSegment(sketch, "E90.MirrorCS", {"start": v(15, -104.25) * mm, "end": v(15, -92.25) * mm});
            skLineSegment(sketch, "E91.MirrorCS", {"start": v(33, -74.25) * mm, "end": v(15, -92.25) * mm});
            skCircle(sketch, "E92.MirrorC", {"center": v(0, -104.25) * mm, "radius": 6 * mm});
            skLineSegment(sketch, "E93.MirrorCS", {"start": v(0, -74.25) * mm, "end": v(0, -104.25) * mm, "construction": true});
            skSolve(sketch);
        }
        {
            var Q0;
            {var subQ0=sQuery(id+"F16.wireOp",EDGE,"E87.MirrorCS");Q0=makeQuery(id+"F16.imprint","IMPRINT",FACE,{"disambiguationData":[TD([[makeQuery(id+"F16.imprint","IMPRINT",EDGE,{"derivedFrom":subQ0}),1.0]])]});}
            var Q1;
            {var subQ0=sQuery(id+"F16.wireOp",EDGE,"E80");Q1=makeQuery(id+"F16.imprint","IMPRINT",FACE,{"disambiguationData":[TD([[makeQuery(id+"F16.imprint","IMPRINT",EDGE,{"derivedFrom":subQ0}),-1.0]])]});}
            var Q2;
            Q2=makeQuery(id+"F16.imprint","IMPRINT",FACE,{"disambiguationData":[TD([[makeQuery(id+"F16.imprint","IMPRINT",EDGE,{"derivedFrom":makeQuery(id+"F1.opExtrude","CAP_EDGE",EDGE,{"disambiguationData":[OSD([sQuery(id+"F0.wireOp",EDGE,"E1.left")])],"isStart":true})}),-1.0]])]});
            var Q3;
            Q3=makeQuery(id+"F2.opExtrude","CAP_FACE",FACE,{"disambiguationData":[OSD([sQuery(id+"F0.wireOp",EDGE,"E12"),sQuery(id+"F0.wireOp",EDGE,"E13"),sQuery(id+"F0.wireOp",EDGE,"E14"),sQuery(id+"F0.wireOp",EDGE,"E15"),sQuery(id+"F0.wireOp",EDGE,"E17.filletArc"),sQuery(id+"F0.wireOp",EDGE,"E18.filletArc"),sQuery(id+"F0.wireOp",EDGE,"E19.filletArc"),sQuery(id+"F0.wireOp",EDGE,"E20.filletArc"),sQuery(id+"F0.wireOp",EDGE,"E25.0"),sQuery(id+"F0.wireOp",EDGE,"E25.1"),sQuery(id+"F0.wireOp",EDGE,"E25.2"),sQuery(id+"F0.wireOp",EDGE,"E25.3"),sQuery(id+"F0.wireOp",EDGE,"E25.4"),sQuery(id+"F0.wireOp",EDGE,"E25.5"),sQuery(id+"F0.wireOp",EDGE,"E25.6"),sQuery(id+"F0.wireOp",EDGE,"E25.7")])],"isStart":false});
            extrude(context, id + "F17", {"entities" : qUnion([Q0, Q1, Q2]), "endBound" : BoundingType.UP_TO_SURFACE, "endBoundEntityFace" : qUnion([Q3]), "depth" : 25 * mm});
        }
    });
